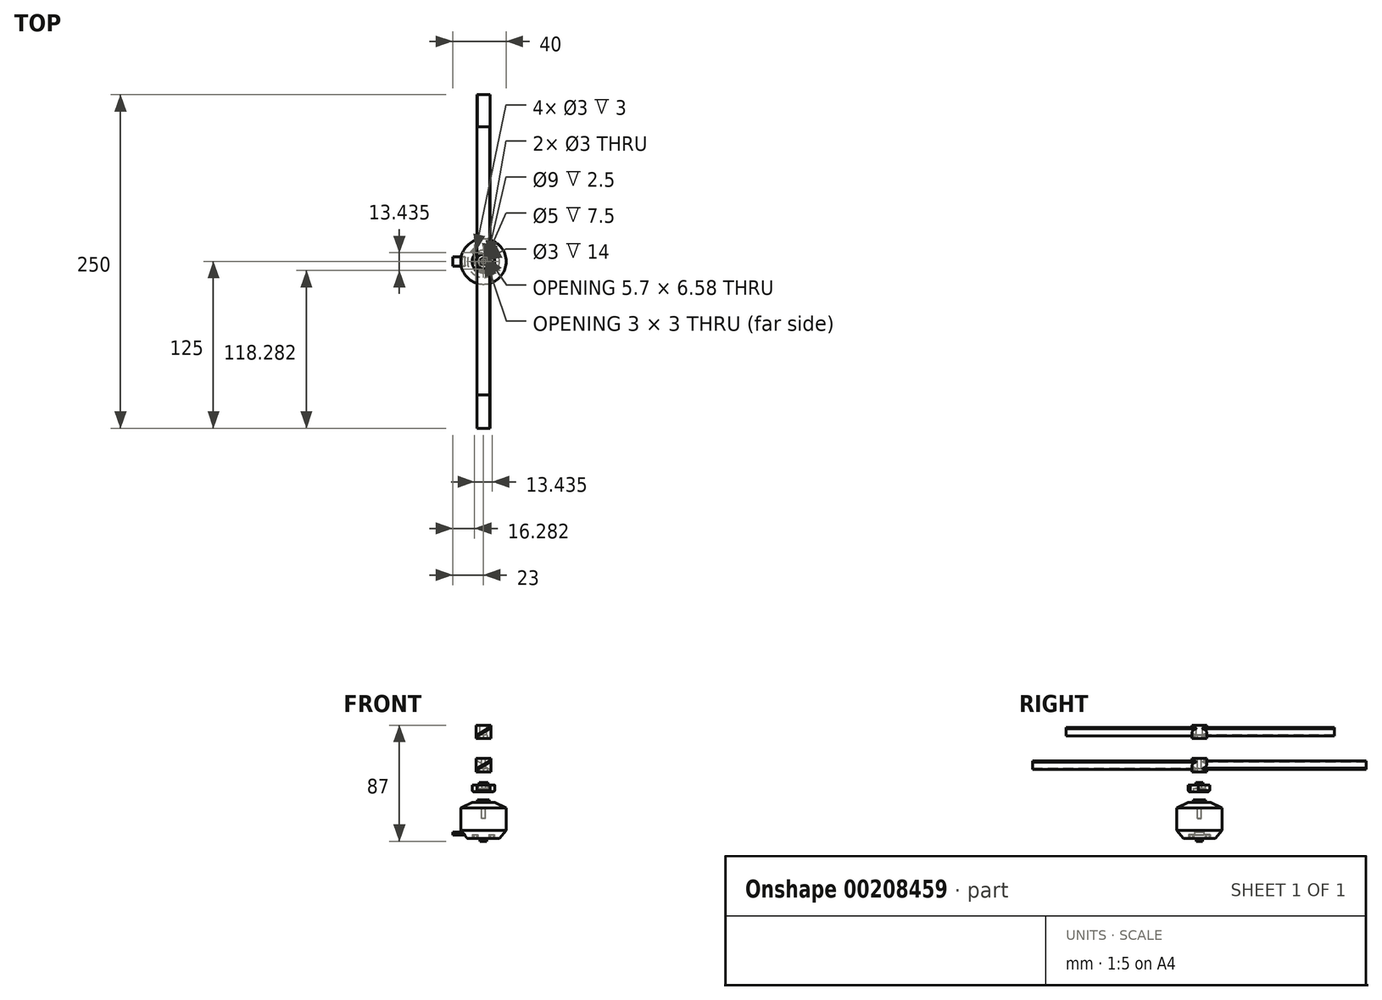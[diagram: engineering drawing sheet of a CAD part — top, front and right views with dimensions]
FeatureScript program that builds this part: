
annotation { "Feature Type Name" : "Feature", "Feature Type Description" : "" }
export const myFeature = defineFeature(function(context is Context, id is Id, definition is map)
    precondition{}
    {
        {
            var Q0;
            Q0=qCreatedBy(makeId("Front.planeOp"),FACE);
            var sketch = newSketch(context, id + "F0", { "sketchPlane" : qUnion([Q0])});
            skLineSegment(sketch, "E0", {"start": v(0, 29) * mm, "end": v(4.5, 29) * mm});
            skLineSegment(sketch, "E1", {"start": v(4.5, 29) * mm, "end": v(4.5, 27) * mm});
            skLineSegment(sketch, "E2", {"start": v(4.5, 27) * mm, "end": v(8.5, 27) * mm});
            skLineSegment(sketch, "E3", {"start": v(8.5, 27) * mm, "end": v(17, 23) * mm});
            skLineSegment(sketch, "E4", {"start": v(17, 23) * mm, "end": v(17, 6) * mm});
            skLineSegment(sketch, "E5", {"start": v(17, 6) * mm, "end": v(12, 0) * mm});
            skLineSegment(sketch, "E6", {"start": v(12, 0) * mm, "end": v(2.5, 0) * mm});
            skLineSegment(sketch, "E7", {"start": v(2.5, 0) * mm, "end": v(2.5, -2) * mm});
            skLineSegment(sketch, "E8", {"start": v(2.5, -2) * mm, "end": v(0, -2) * mm});
            skLineSegment(sketch, "E9", {"start": v(0, -2) * mm, "end": v(0, 29) * mm});
            skSolve(sketch);
        }
        {
            var Q0;
            Q0=makeQuery(id+"F0.imprint","IMPRINT",FACE,{"disambiguationData":[TD([[makeQuery(id+"F0.imprint","IMPRINT",EDGE,{"derivedFrom":sQuery(id+"F0.wireOp",EDGE,"E0")}),-1.0]])]});
            var Q1;
            Q1=sQuery(id+"F0.wireOp",EDGE,"E9");
            revolve(context, id + "F1", {"entities" : qUnion([Q0]), "axis" : qUnion([Q1]), "revolveType" : RevolveType.FULL});
        }
        {
            var Q0;
            Q0=makeQuery(id+"F1.opRevolve","SWEPT_FACE",FACE,{"disambiguationData":[OSD([sQuery(id+"F0.wireOp",EDGE,"E6")])]});
            var sketch = newSketch(context, id + "F2", { "sketchPlane" : qUnion([Q0])});
            skCircle(sketch, "E10", {"center": v(-5.66, 5.66) * mm, "radius": 1.5 * mm});
            skCircle(sketch, "E11", {"center": v(5.66, -5.66) * mm, "radius": 1.5 * mm});
            skCircle(sketch, "E12", {"center": v(6.72, 6.72) * mm, "radius": 1.5 * mm});
            skCircle(sketch, "E13", {"center": v(-6.72, -6.72) * mm, "radius": 1.5 * mm});
            skLineSegment(sketch, "E14", {"start": v(-6.72, -6.72) * mm, "end": v(6.72, 6.72) * mm, "construction": true});
            skLineSegment(sketch, "E15", {"start": v(-5.66, 5.66) * mm, "end": v(5.66, -5.66) * mm, "construction": true});
            skSolve(sketch);
        }
        {
            var Q0;
            Q0=makeQuery(id+"F2.imprint","IMPRINT",FACE,{"disambiguationData":[TD([[makeQuery(id+"F2.imprint","IMPRINT",EDGE,{"derivedFrom":sQuery(id+"F2.wireOp",EDGE,"E10")}),1.0]])]});
            var Q1;
            Q1=makeQuery(id+"F2.imprint","IMPRINT",FACE,{"disambiguationData":[TD([[makeQuery(id+"F2.imprint","IMPRINT",EDGE,{"derivedFrom":sQuery(id+"F2.wireOp",EDGE,"E13")}),1.0]])]});
            var Q2;
            Q2=makeQuery(id+"F2.imprint","IMPRINT",FACE,{"disambiguationData":[TD([[makeQuery(id+"F2.imprint","IMPRINT",EDGE,{"derivedFrom":sQuery(id+"F2.wireOp",EDGE,"E11")}),1.0]])]});
            var Q3;
            Q3=makeQuery(id+"F2.imprint","IMPRINT",FACE,{"disambiguationData":[TD([[makeQuery(id+"F2.imprint","IMPRINT",EDGE,{"derivedFrom":sQuery(id+"F2.wireOp",EDGE,"E12")}),1.0]])]});
            extrude(context, id + "F3", {"entities" : qUnion([Q0, Q1, Q2, Q3]), "operationType" : NewBodyOperationType.REMOVE, "oppositeDirection" : true, "depth" : 3 * mm});
        }
        {
            var Q0;
            Q0=makeQuery(id+"F1.opRevolve","SWEPT_FACE",FACE,{"disambiguationData":[OSD([sQuery(id+"F0.wireOp",EDGE,"E6")])]});
            var sketch = newSketch(context, id + "F4", { "sketchPlane" : qUnion([Q0])});
            skLineSegment(sketch, "E16.bottom", {"start": v(-13, -3.5) * mm, "end": v(-23, -3.5) * mm});
            skLineSegment(sketch, "E16.top", {"start": v(-13, 3.5) * mm, "end": v(-23, 3.5) * mm});
            skLineSegment(sketch, "E16.left", {"start": v(-13, -3.5) * mm, "end": v(-13, 3.5) * mm});
            skLineSegment(sketch, "E16.right", {"start": v(-23, -3.5) * mm, "end": v(-23, 3.5) * mm});
            skSolve(sketch);
        }
        {
            var Q0;
            Q0=makeQuery(id+"F4.imprint","IMPRINT",FACE,{"disambiguationData":[TD([[makeQuery(id+"F4.imprint","IMPRINT",EDGE,{"derivedFrom":sQuery(id+"F4.wireOp",EDGE,"E16.bottom")}),-1.0]])]});
            extrude(context, id + "F5", {"entities" : qUnion([Q0]), "operationType" : NewBodyOperationType.ADD, "oppositeDirection" : true, "depth" : 5 * mm, "hasSecondDirection" : true, "secondDirectionOppositeDirection" : true, "secondDirectionDepth" : 2.5 * mm});
        }
        {
            var Q0;
            Q0=qCreatedBy(makeId("Front.planeOp"),FACE);
            var sketch = newSketch(context, id + "F6", { "sketchPlane" : qUnion([Q0])});
            skLineSegment(sketch, "E17", {"start": v(-8.5, 40) * mm, "end": v(-8.5, 36) * mm});
            skLineSegment(sketch, "E18", {"start": v(-8.5, 36) * mm, "end": v(-7.5, 35) * mm});
            skLineSegment(sketch, "E19", {"start": v(-7.5, 35) * mm, "end": v(0, 35) * mm});
            skLineSegment(sketch, "E20", {"start": v(0, 35) * mm, "end": v(0, 40) * mm});
            skLineSegment(sketch, "E21", {"start": v(0, 40) * mm, "end": v(-8.5, 40) * mm});
            skLineSegment(sketch, "E22", {"start": v(-4.5, 35) * mm, "end": v(-4.5, 37.5) * mm});
            skLineSegment(sketch, "E23", {"start": v(-4.5, 37.5) * mm, "end": v(0, 37.5) * mm});
            skSolve(sketch);
        }
        {
            var Q0;
            Q0=makeQuery(id+"F6.imprint","IMPRINT",FACE,{"disambiguationData":[TD([[makeQuery(id+"F6.imprint","IMPRINT",EDGE,{"derivedFrom":sQuery(id+"F6.wireOp",EDGE,"E17")}),1.0]])]});
            var Q1;
            Q1=sQuery(id+"F6.wireOp",EDGE,"E20");
            revolve(context, id + "F7", {"entities" : qUnion([Q0]), "axis" : qUnion([Q1]), "revolveType" : RevolveType.FULL});
        }
        {
            var Q0;
            Q0=makeQuery(id+"F7.opRevolve","SWEPT_FACE",FACE,{"disambiguationData":[OSD([sQuery(id+"F6.wireOp",EDGE,"E21")])]});
            var sketch = newSketch(context, id + "F8", { "sketchPlane" : qUnion([Q0])});
            skCircle(sketch, "E24", {"center": v(0, 8.05) * mm, "radius": 3.5 * mm});
            skCircle(sketch, "E25", {"center": v(0, 0) * mm, "radius": 4.55 * mm, "construction": true});
            skCircle(sketch, "E26.1.0", {"center": v(-6.97, -4.02) * mm, "radius": 3.5 * mm});
            skCircle(sketch, "E26.2.0", {"center": v(6.97, -4.02) * mm, "radius": 3.5 * mm});
            skCircle(sketch, "E27.cCircle", {"center": v(0, 0) * mm, "radius": 3.26 * mm, "construction": true});
            skLineSegment(sketch, "E27.0", {"start": v(-3.26, 0) * mm, "end": v(-1.63, 2.82) * mm});
            skLineSegment(sketch, "E27.1", {"start": v(-1.63, 2.82) * mm, "end": v(1.63, 2.83) * mm});
            skLineSegment(sketch, "E27.2", {"start": v(1.63, 2.83) * mm, "end": v(3.26, 0) * mm});
            skLineSegment(sketch, "E27.3", {"start": v(3.26, 0) * mm, "end": v(1.63, -2.82) * mm});
            skLineSegment(sketch, "E27.4", {"start": v(1.63, -2.82) * mm, "end": v(-1.63, -2.83) * mm});
            skLineSegment(sketch, "E27.5", {"start": v(-1.63, -2.83) * mm, "end": v(-3.26, 0) * mm});
            skCircle(sketch, "E28", {"center": v(0, 0) * mm, "radius": 1.5 * mm});
            skSolve(sketch);
        }
        {
            var Q0;
            {var subQ0=sQuery(id+"F8.wireOp",EDGE,"E26.1.0");var subQ1=makeQuery(id+"F7.opRevolve","SWEPT_EDGE",EDGE,{"disambiguationData":[OSD([sQuery(id+"F6.wireOp",EDGE,"E17"),sQuery(id+"F6.wireOp",EDGE,"E21")])]});var subQ2=makeQuery(id+"F8.imprint","INTERSECT",VERTEX,{"disambiguationData":[OD(0.0)],"derivedFrom":[subQ1,subQ0]});Q0=makeQuery(id+"F8.imprint","IMPRINT",FACE,{"disambiguationData":[TD([[makeQuery(id+"F8.imprint","IMPRINT",EDGE,{"disambiguationData":[TD([[subQ2,1.0]])],"derivedFrom":subQ0}),1.0]])]});}
            var Q1;
            {var subQ0=sQuery(id+"F8.wireOp",EDGE,"E24");var subQ1=makeQuery(id+"F7.opRevolve","SWEPT_EDGE",EDGE,{"disambiguationData":[OSD([sQuery(id+"F6.wireOp",EDGE,"E17"),sQuery(id+"F6.wireOp",EDGE,"E21")])]});var subQ2=makeQuery(id+"F8.imprint","INTERSECT",VERTEX,{"disambiguationData":[OD(0.0)],"derivedFrom":[subQ1,subQ0]});Q1=makeQuery(id+"F8.imprint","IMPRINT",FACE,{"disambiguationData":[TD([[makeQuery(id+"F8.imprint","IMPRINT",EDGE,{"disambiguationData":[TD([[subQ2,-1.0]])],"derivedFrom":subQ0}),1.0]])]});}
            var Q2;
            {var subQ0=sQuery(id+"F8.wireOp",EDGE,"E26.2.0");var subQ1=makeQuery(id+"F7.opRevolve","SWEPT_EDGE",EDGE,{"disambiguationData":[OSD([sQuery(id+"F6.wireOp",EDGE,"E17"),sQuery(id+"F6.wireOp",EDGE,"E21")])]});var subQ2=makeQuery(id+"F8.imprint","INTERSECT",VERTEX,{"disambiguationData":[OD(0.0)],"derivedFrom":[subQ1,subQ0]});Q2=makeQuery(id+"F8.imprint","IMPRINT",FACE,{"disambiguationData":[TD([[makeQuery(id+"F8.imprint","IMPRINT",EDGE,{"disambiguationData":[TD([[subQ2,1.0]])],"derivedFrom":subQ0}),1.0]])]});}
            var Q3;
            Q3=makeQuery(id+"F7.opRevolve","SWEPT_FACE",FACE,{"disambiguationData":[OSD([sQuery(id+"F6.wireOp",EDGE,"E19")])]});
            extrude(context, id + "F9", {"entities" : qUnion([Q0, Q1, Q2]), "operationType" : NewBodyOperationType.REMOVE, "endBound" : BoundingType.UP_TO_SURFACE, "oppositeDirection" : true, "endBoundEntityFace" : qUnion([Q3]), "depth" : 25 * mm});
        }
        {
            var Q0;
            Q0=makeQuery(id+"F8.imprint","IMPRINT",FACE,{"disambiguationData":[TD([[makeQuery(id+"F8.imprint","IMPRINT",EDGE,{"derivedFrom":sQuery(id+"F8.wireOp",EDGE,"E27.0")}),-1.0]])]});
            extrude(context, id + "F10", {"entities" : qUnion([Q0]), "operationType" : NewBodyOperationType.ADD, "depth" : 2 * mm});
        }
        {
            var Q0;
            Q0=makeQuery(id+"F8.imprint","IMPRINT",FACE,{"disambiguationData":[TD([[makeQuery(id+"F8.imprint","IMPRINT",EDGE,{"derivedFrom":sQuery(id+"F8.wireOp",EDGE,"E28")}),1.0]])]});
            extrude(context, id + "F11", {"entities" : qUnion([Q0]), "operationType" : NewBodyOperationType.REMOVE, "oppositeDirection" : true, "depth" : 25 * mm});
        }
        {
            var Q0;
            Q0=qCreatedBy(makeId("Front.planeOp"),FACE);
            var sketch = newSketch(context, id + "F12", { "sketchPlane" : qUnion([Q0])});
            skLineSegment(sketch, "E29", {"start": v(-5.5, 50) * mm, "end": v(-5.5, 60) * mm});
            skLineSegment(sketch, "E30", {"start": v(-5.5, 60) * mm, "end": v(0, 60) * mm});
            skLineSegment(sketch, "E31", {"start": v(0, 60) * mm, "end": v(0, 50) * mm});
            skLineSegment(sketch, "E32", {"start": v(-1.5, 60) * mm, "end": v(-1.5, 50) * mm});
            skLineSegment(sketch, "E33", {"start": v(-5.5, 50) * mm, "end": v(0, 50) * mm});
            skSolve(sketch);
        }
        {
            var Q0;
            {var subQ1=sQuery(id+"F12.wireOp",EDGE,"Nvnc9InG-rB4M-fcRY-kVf7-8wGeuTWhSEZq");Q0=makeQuery(id+"F12.imprint","IMPRINT",FACE,{"disambiguationData":[TD([[makeQuery(id+"F12.imprint","IMPRINT",EDGE,{"derivedFrom":subQ1}),-1.0]])]});}
            var Q1;
            {var subQ0=sQuery(id+"F12.wireOp",EDGE,"E29");Q1=makeQuery(id+"F12.imprint","IMPRINT",FACE,{"disambiguationData":[TD([[makeQuery(id+"F12.imprint","IMPRINT",EDGE,{"derivedFrom":subQ0}),-1.0]])]});}
            var Q2;
            Q2=sQuery(id+"F12.wireOp",EDGE,"E31");
            revolve(context, id + "F13", {"entities" : qUnion([Q0, Q1]), "axis" : qUnion([Q2]), "revolveType" : RevolveType.FULL});
        }
        {
            var Q0;
            Q0=qCreatedBy(makeId("Front.planeOp"),FACE);
            var sketch = newSketch(context, id + "F14", { "sketchPlane" : qUnion([Q0])});
            skLineSegment(sketch, "E34", {"start": v(-5.01, 52.68) * mm, "end": v(-4.51, 51.82) * mm});
            skLineSegment(sketch, "E35", {"start": v(-4.51, 51.82) * mm, "end": v(5.01, 57.32) * mm});
            skLineSegment(sketch, "E36", {"start": v(5.01, 57.32) * mm, "end": v(4.51, 58.18) * mm});
            skLineSegment(sketch, "E37", {"start": v(4.51, 58.18) * mm, "end": v(-5.01, 52.68) * mm});
            skLineSegment(sketch, "E38", {"start": v(0, 55.58) * mm, "end": v(0, 54.42) * mm, "construction": true});
            skLineSegment(sketch, "E39", {"start": v(-4.76, 52.25) * mm, "end": v(4.76, 57.75) * mm, "construction": true});
            skLineSegment(sketch, "E40", {"start": v(-0.25, 55.43) * mm, "end": v(0.25, 54.57) * mm, "construction": true});
            skPoint(sketch, "E41", {"position": v(0, 55) * mm});
            skLineSegment(sketch, "E42", {"start": v(1, 55) * mm, "end": v(-1, 55) * mm, "construction": true});
            skLineSegment(sketch, "E43.MirrorCS", {"start": v(-4.51, 58.18) * mm, "end": v(5.01, 52.68) * mm});
            skLineSegment(sketch, "E44.MirrorCS", {"start": v(4.51, 51.82) * mm, "end": v(-5.01, 57.32) * mm});
            skLineSegment(sketch, "E45.MirrorCS", {"start": v(-5.01, 57.32) * mm, "end": v(-4.51, 58.18) * mm});
            skLineSegment(sketch, "E46.MirrorCS", {"start": v(5.01, 52.68) * mm, "end": v(4.51, 51.82) * mm});
            skSolve(sketch);
        }
        {
            var Q0;
            Q0=makeQuery(id+"F14.imprint","IMPRINT",FACE,{"disambiguationData":[TD([[makeQuery(id+"F14.imprint","IMPRINT",EDGE,{"derivedFrom":sQuery(id+"F14.wireOp",EDGE,"E34")}),1.0]])]});
            var Q1;
            {var subQ0=sQuery(id+"F14.wireOp",EDGE,"E44.MirrorCS");var subQ1=sQuery(id+"F14.wireOp",EDGE,"E35");var subQ2=makeQuery(id+"F14.imprint","INTERSECT",VERTEX,{"derivedFrom":[subQ1,subQ0]});Q1=makeQuery(id+"F14.imprint","IMPRINT",FACE,{"disambiguationData":[TD([[makeQuery(id+"F14.imprint","IMPRINT",EDGE,{"disambiguationData":[TD([[subQ2,-1.0]])],"derivedFrom":subQ1}),1.0]])]});}
            var Q2;
            {var subQ0=sQuery(id+"F14.wireOp",EDGE,"E36");Q2=makeQuery(id+"F14.imprint","IMPRINT",FACE,{"disambiguationData":[TD([[makeQuery(id+"F14.imprint","IMPRINT",EDGE,{"derivedFrom":subQ0}),1.0]])]});}
            extrude(context, id + "F15", {"entities" : qUnion([Q0, Q1, Q2]), "operationType" : NewBodyOperationType.ADD, "depth" : 125 * mm});
        }
        {
            var Q0;
            {var subQ5=sQuery(id+"F14.wireOp",EDGE,"E46.MirrorCS");Q0=makeQuery(id+"F14.imprint","IMPRINT",FACE,{"disambiguationData":[TD([[makeQuery(id+"F14.imprint","IMPRINT",EDGE,{"derivedFrom":subQ5}),-1.0]])]});}
            var Q1;
            {var subQ0=sQuery(id+"F14.wireOp",EDGE,"E44.MirrorCS");var subQ1=sQuery(id+"F14.wireOp",EDGE,"E35");var subQ2=makeQuery(id+"F14.imprint","INTERSECT",VERTEX,{"derivedFrom":[subQ1,subQ0]});Q1=makeQuery(id+"F14.imprint","IMPRINT",FACE,{"disambiguationData":[TD([[makeQuery(id+"F14.imprint","IMPRINT",EDGE,{"disambiguationData":[TD([[subQ2,-1.0]])],"derivedFrom":subQ1}),1.0]])]});}
            var Q2;
            {var subQ5=sQuery(id+"F14.wireOp",EDGE,"E45.MirrorCS");Q2=makeQuery(id+"F14.imprint","IMPRINT",FACE,{"disambiguationData":[TD([[makeQuery(id+"F14.imprint","IMPRINT",EDGE,{"derivedFrom":subQ5}),-1.0]])]});}
            extrude(context, id + "F16", {"entities" : qUnion([Q0, Q1, Q2]), "operationType" : NewBodyOperationType.ADD, "oppositeDirection" : true, "depth" : 125 * mm});
        }
        {
            var Q0;
            Q0=makeQuery(id+"F13.opRevolve","SWEPT_FACE",FACE,{"disambiguationData":[OSD([sQuery(id+"F12.wireOp",EDGE,"E33")])]});
            var sketch = newSketch(context, id + "F17", { "sketchPlane" : qUnion([Q0])});
            skCircle(sketch, "E47.cCircle", {"center": v(0, 0) * mm, "radius": 3.3 * mm, "construction": true});
            skLineSegment(sketch, "E47.0", {"start": v(0, -3.3) * mm, "end": v(-2.85, -1.65) * mm});
            skLineSegment(sketch, "E47.1", {"start": v(-2.85, -1.65) * mm, "end": v(-2.85, 1.65) * mm});
            skLineSegment(sketch, "E47.2", {"start": v(-2.85, 1.65) * mm, "end": v(0, 3.3) * mm});
            skLineSegment(sketch, "E47.3", {"start": v(0, 3.3) * mm, "end": v(2.85, 1.65) * mm});
            skLineSegment(sketch, "E47.4", {"start": v(2.85, 1.65) * mm, "end": v(2.85, -1.65) * mm});
            skLineSegment(sketch, "E47.5", {"start": v(2.85, -1.65) * mm, "end": v(0, -3.3) * mm});
            skCircle(sketch, "E48", {"center": v(0, 0) * mm, "radius": 1.5 * mm});
            skSolve(sketch);
        }
        {
            var Q0;
            Q0=makeQuery(id+"F17.imprint","IMPRINT",FACE,{"disambiguationData":[TD([[makeQuery(id+"F17.imprint","IMPRINT",EDGE,{"derivedFrom":sQuery(id+"F17.wireOp",EDGE,"E47.0")}),-1.0]])]});
            var Q1;
            Q1=makeQuery(id+"F17.imprint","IMPRINT",FACE,{"disambiguationData":[TD([[makeQuery(id+"F17.imprint","IMPRINT",EDGE,{"derivedFrom":sQuery(id+"F17.wireOp",EDGE,"E48")}),-1.0]])]});
            extrude(context, id + "F18", {"entities" : qUnion([Q0, Q1]), "operationType" : NewBodyOperationType.REMOVE, "oppositeDirection" : true, "depth" : 2.5 * mm});
        }
        {
            var Q0;
            Q0=makeQuery(id+"F17.imprint","IMPRINT",FACE,{"disambiguationData":[TD([[makeQuery(id+"F17.imprint","IMPRINT",EDGE,{"derivedFrom":sQuery(id+"F17.wireOp",EDGE,"E48")}),-1.0]])]});
            extrude(context, id + "F19", {"entities" : qUnion([Q0]), "operationType" : NewBodyOperationType.REMOVE, "oppositeDirection" : true, "depth" : 25 * mm});
        }
        {
            var Q0;
            Q0=qCreatedBy(makeId("Front.planeOp"),FACE);
            var sketch = newSketch(context, id + "F20", { "sketchPlane" : qUnion([Q0])});
            skLineSegment(sketch, "E49", {"start": v(-5.5, 75) * mm, "end": v(-5.5, 85) * mm});
            skLineSegment(sketch, "E50", {"start": v(-5.5, 85) * mm, "end": v(0, 85) * mm});
            skLineSegment(sketch, "E51", {"start": v(0, 85) * mm, "end": v(0, 75) * mm});
            skLineSegment(sketch, "E52", {"start": v(-2.5, 85) * mm, "end": v(-2.5, 75) * mm});
            skLineSegment(sketch, "E53", {"start": v(-5.5, 75) * mm, "end": v(0, 75) * mm});
            skSolve(sketch);
        }
        {
            var Q0;
            {var subQ0=sQuery(id+"F20.wireOp",EDGE,"E49");Q0=makeQuery(id+"F20.imprint","IMPRINT",FACE,{"disambiguationData":[TD([[makeQuery(id+"F20.imprint","IMPRINT",EDGE,{"derivedFrom":subQ0}),-1.0]])]});}
            var Q1;
            Q1=sQuery(id+"F20.wireOp",EDGE,"E51");
            revolve(context, id + "F21", {"entities" : qUnion([Q0]), "axis" : qUnion([Q1]), "revolveType" : RevolveType.FULL});
        }
        {
            var Q0;
            Q0=qCreatedBy(makeId("Front.planeOp"),FACE);
            var sketch = newSketch(context, id + "F22", { "sketchPlane" : qUnion([Q0])});
            skLineSegment(sketch, "E54", {"start": v(-5.01, 77.68) * mm, "end": v(-4.51, 76.82) * mm});
            skLineSegment(sketch, "E55", {"start": v(-4.51, 76.82) * mm, "end": v(5.01, 82.32) * mm});
            skLineSegment(sketch, "E56", {"start": v(5.01, 82.32) * mm, "end": v(4.51, 83.18) * mm});
            skLineSegment(sketch, "E57", {"start": v(4.51, 83.18) * mm, "end": v(-5.01, 77.68) * mm});
            skLineSegment(sketch, "E58", {"start": v(0, 80.58) * mm, "end": v(0, 79.42) * mm, "construction": true});
            skLineSegment(sketch, "E59", {"start": v(-4.76, 77.25) * mm, "end": v(4.76, 82.75) * mm, "construction": true});
            skLineSegment(sketch, "E60", {"start": v(-0.25, 80.43) * mm, "end": v(0.25, 79.57) * mm, "construction": true});
            skPoint(sketch, "E61", {"position": v(0, 80) * mm});
            skLineSegment(sketch, "E62", {"start": v(1, 80) * mm, "end": v(-1, 80) * mm, "construction": true});
            skLineSegment(sketch, "E63.MirrorCS", {"start": v(-4.51, 83.18) * mm, "end": v(5.01, 77.68) * mm});
            skLineSegment(sketch, "E64.MirrorCS", {"start": v(4.51, 76.82) * mm, "end": v(-5.01, 82.32) * mm});
            skLineSegment(sketch, "E65.MirrorCS", {"start": v(-5.01, 82.32) * mm, "end": v(-4.51, 83.18) * mm});
            skLineSegment(sketch, "E66.MirrorCS", {"start": v(5.01, 77.68) * mm, "end": v(4.51, 76.82) * mm});
            skSolve(sketch);
        }
        {
            var Q0;
            {var subQ0=sQuery(id+"F22.wireOp",EDGE,"E56");Q0=makeQuery(id+"F22.imprint","IMPRINT",FACE,{"disambiguationData":[TD([[makeQuery(id+"F22.imprint","IMPRINT",EDGE,{"derivedFrom":subQ0}),1.0]])]});}
            var Q1;
            {var subQ0=sQuery(id+"F22.wireOp",EDGE,"E64.MirrorCS");var subQ1=sQuery(id+"F22.wireOp",EDGE,"E55");var subQ2=makeQuery(id+"F22.imprint","INTERSECT",VERTEX,{"derivedFrom":[subQ1,subQ0]});Q1=makeQuery(id+"F22.imprint","IMPRINT",FACE,{"disambiguationData":[TD([[makeQuery(id+"F22.imprint","IMPRINT",EDGE,{"disambiguationData":[TD([[subQ2,-1.0]])],"derivedFrom":subQ1}),1.0]])]});}
            var Q2;
            {var subQ0=sQuery(id+"F22.wireOp",EDGE,"E54");Q2=makeQuery(id+"F22.imprint","IMPRINT",FACE,{"disambiguationData":[TD([[makeQuery(id+"F22.imprint","IMPRINT",EDGE,{"derivedFrom":subQ0}),1.0]])]});}
            extrude(context, id + "F23", {"entities" : qUnion([Q0, Q1, Q2]), "operationType" : NewBodyOperationType.ADD, "oppositeDirection" : true, "depth" : 101 * mm});
        }
        {
            var Q0;
            {var subQ0=sQuery(id+"F22.wireOp",EDGE,"E54");Q0=makeQuery(id+"F22.imprint","IMPRINT",FACE,{"disambiguationData":[TD([[makeQuery(id+"F22.imprint","IMPRINT",EDGE,{"derivedFrom":subQ0}),1.0]])]});}
            var Q1;
            {var subQ0=sQuery(id+"F22.wireOp",EDGE,"E64.MirrorCS");var subQ1=sQuery(id+"F22.wireOp",EDGE,"E55");var subQ2=makeQuery(id+"F22.imprint","INTERSECT",VERTEX,{"derivedFrom":[subQ1,subQ0]});Q1=makeQuery(id+"F22.imprint","IMPRINT",FACE,{"disambiguationData":[TD([[makeQuery(id+"F22.imprint","IMPRINT",EDGE,{"disambiguationData":[TD([[subQ2,-1.0]])],"derivedFrom":subQ1}),1.0]])]});}
            var Q2;
            {var subQ0=sQuery(id+"F22.wireOp",EDGE,"E56");Q2=makeQuery(id+"F22.imprint","IMPRINT",FACE,{"disambiguationData":[TD([[makeQuery(id+"F22.imprint","IMPRINT",EDGE,{"derivedFrom":subQ0}),1.0]])]});}
            extrude(context, id + "F24", {"entities" : qUnion([Q0, Q1, Q2]), "operationType" : NewBodyOperationType.ADD, "depth" : 100 * mm});
        }
        {
            var Q0;
            Q0=makeQuery(id+"F21.opRevolve","SWEPT_FACE",FACE,{"disambiguationData":[OSD([sQuery(id+"F20.wireOp",EDGE,"E53")])]});
            var sketch = newSketch(context, id + "F25", { "sketchPlane" : qUnion([Q0])});
            skCircle(sketch, "E67.cCircle", {"center": v(0, 0) * mm, "radius": 3.3 * mm, "construction": true});
            skLineSegment(sketch, "E67.0", {"start": v(0, -3.3) * mm, "end": v(-2.85, -1.65) * mm});
            skLineSegment(sketch, "E67.1", {"start": v(-2.85, -1.65) * mm, "end": v(-2.85, 1.65) * mm});
            skLineSegment(sketch, "E67.2", {"start": v(-2.85, 1.65) * mm, "end": v(0, 3.3) * mm});
            skLineSegment(sketch, "E67.3", {"start": v(0, 3.3) * mm, "end": v(2.85, 1.65) * mm});
            skLineSegment(sketch, "E67.4", {"start": v(2.85, 1.65) * mm, "end": v(2.85, -1.65) * mm});
            skLineSegment(sketch, "E67.5", {"start": v(2.85, -1.65) * mm, "end": v(0, -3.3) * mm});
            skCircle(sketch, "E68", {"center": v(0, 0) * mm, "radius": 2.5 * mm});
            skSolve(sketch);
        }
        {
            var Q0;
            Q0=makeQuery(id+"F25.imprint","IMPRINT",FACE,{"disambiguationData":[TD([[makeQuery(id+"F25.imprint","IMPRINT",EDGE,{"derivedFrom":sQuery(id+"F25.wireOp",EDGE,"E67.0")}),-1.0]])]});
            extrude(context, id + "F26", {"entities" : qUnion([Q0]), "operationType" : NewBodyOperationType.REMOVE, "oppositeDirection" : true, "depth" : 2.5 * mm});
        }
        {
            var Q0;
            Q0=makeQuery(id+"F25.imprint","IMPRINT",FACE,{"disambiguationData":[TD([[makeQuery(id+"F25.imprint","IMPRINT",EDGE,{"derivedFrom":sQuery(id+"F25.wireOp",EDGE,"E68")}),-1.0]])]});
            extrude(context, id + "F27", {"entities" : qUnion([Q0]), "operationType" : NewBodyOperationType.REMOVE, "oppositeDirection" : true, "depth" : 25 * mm});
        }
    });
